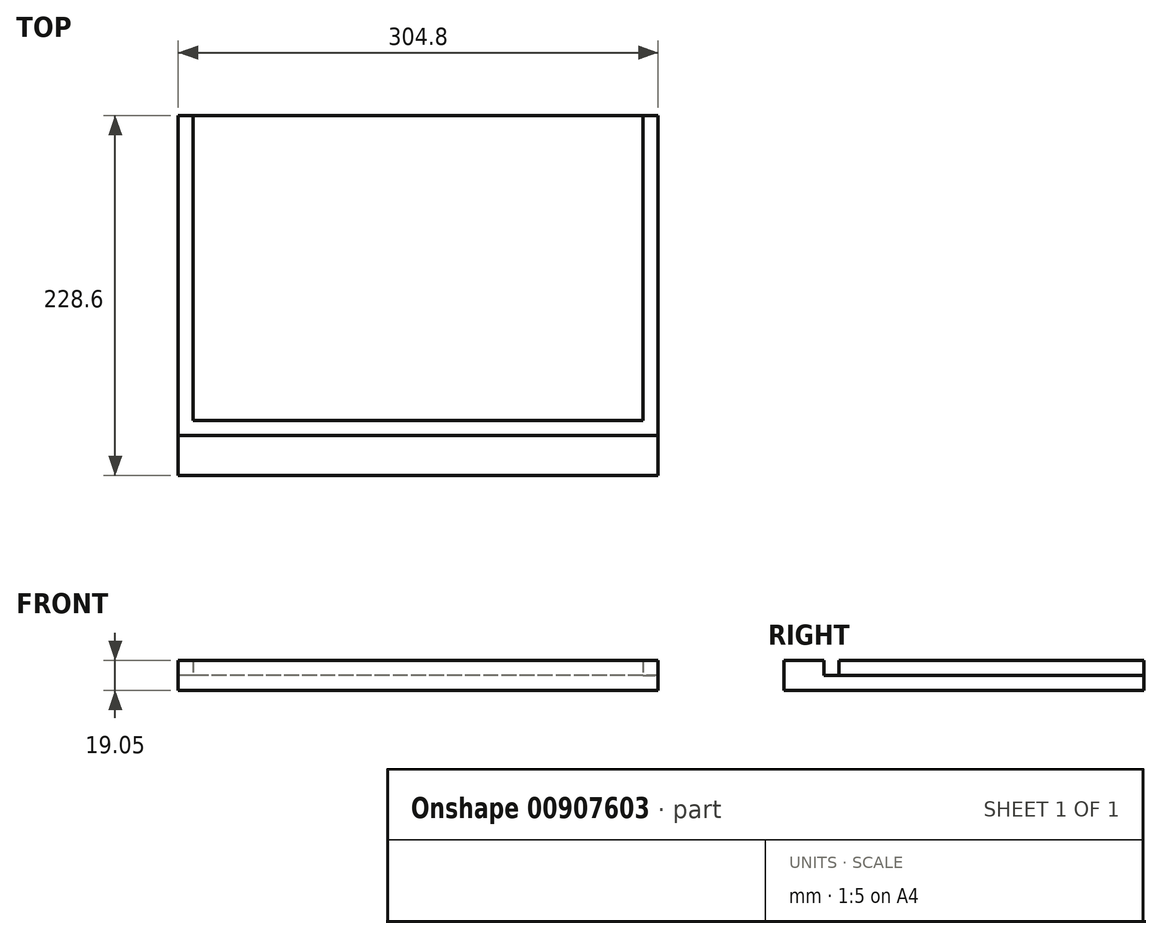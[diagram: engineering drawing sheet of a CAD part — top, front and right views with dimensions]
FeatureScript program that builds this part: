
annotation { "Feature Type Name" : "Feature", "Feature Type Description" : "" }
export const myFeature = defineFeature(function(context is Context, id is Id, definition is map)
    precondition{}
    {
        {
            var Q0;
            Q0=qCreatedBy(makeId("Top.planeOp"),FACE);
            var sketch = newSketch(context, id + "F0", { "sketchPlane" : qUnion([Q0])});
            skLineSegment(sketch, "E0.bottom", {"start": v(152.4, -114.3) * mm, "end": v(-152.4, -114.3) * mm});
            skLineSegment(sketch, "E0.top", {"start": v(152.4, 114.3) * mm, "end": v(-152.4, 114.3) * mm});
            skLineSegment(sketch, "E0.left", {"start": v(152.4, -114.3) * mm, "end": v(152.4, 114.3) * mm});
            skLineSegment(sketch, "E0.right", {"start": v(-152.4, -114.3) * mm, "end": v(-152.4, 114.3) * mm});
            skPoint(sketch, "E0.middle", {"position": v(0, 0) * mm});
            skSolve(sketch);
        }
        {
            var Q0;
            Q0=qSketchRegion(id+"F0",true);
            extrude(context, id + "F1", {"entities" : qUnion([Q0]), "depth" : 19.05 * mm, "offsetDistance" : 25.4 * mm});
        }
        {
            var Q0;
            Q0=makeQuery(id+"F1.opExtrude","CAP_FACE",FACE,{"disambiguationData":[OSD([sQuery(id+"F0.wireOp",EDGE,"E0.bottom"),sQuery(id+"F0.wireOp",EDGE,"E0.top"),sQuery(id+"F0.wireOp",EDGE,"E0.left"),sQuery(id+"F0.wireOp",EDGE,"E0.right")])],"isStart":false});
            var sketch = newSketch(context, id + "F2", { "sketchPlane" : qUnion([Q0])});
            skLineSegment(sketch, "E1", {"start": v(0, -114.3) * mm, "end": v(0, -84.14) * mm});
            skLineSegment(sketch, "E2.bottom", {"start": v(188.14, -79.38) * mm, "end": v(-188.14, -79.38) * mm});
            skLineSegment(sketch, "E2.top", {"start": v(188.14, -88.9) * mm, "end": v(-188.14, -88.9) * mm});
            skLineSegment(sketch, "E2.left", {"start": v(188.14, -79.38) * mm, "end": v(188.14, -88.9) * mm});
            skLineSegment(sketch, "E2.right", {"start": v(-188.14, -79.38) * mm, "end": v(-188.14, -88.9) * mm});
            skPoint(sketch, "E2.middle", {"position": v(0, -84.14) * mm});
            skSolve(sketch);
        }
        {
            var Q0;
            Q0=qSketchRegion(id+"F2",true);
            extrude(context, id + "F3", {"entities" : qUnion([Q0]), "operationType" : NewBodyOperationType.REMOVE, "oppositeDirection" : true, "depth" : 9.52 * mm, "offsetDistance" : 25.4 * mm});
        }
        {
            var Q0;
            Q0=makeQuery(id+"F1.opExtrude","SWEPT_FACE",FACE,{"disambiguationData":[OSD([sQuery(id+"F0.wireOp",EDGE,"E0.right")])]});
            var sketch = newSketch(context, id + "F4", { "sketchPlane" : qUnion([Q0])});
            skLineSegment(sketch, "E3.bottom", {"start": v(79.38, 28.57) * mm, "end": v(-114.3, 28.57) * mm});
            skLineSegment(sketch, "E3.top", {"start": v(79.38, 9.53) * mm, "end": v(-114.3, 9.53) * mm});
            skLineSegment(sketch, "E3.left", {"start": v(79.38, 28.57) * mm, "end": v(79.38, 9.53) * mm});
            skLineSegment(sketch, "E3.right", {"start": v(-114.3, 28.57) * mm, "end": v(-114.3, 9.53) * mm});
            skPoint(sketch, "E3.middle", {"position": v(-17.46, 19.05) * mm});
            skSolve(sketch);
        }
        {
            var Q0;
            Q0=qSketchRegion(id+"F4",true);
            extrude(context, id + "F5", {"entities" : qUnion([Q0]), "operationType" : NewBodyOperationType.REMOVE, "oppositeDirection" : true, "depth" : 9.52 * mm, "offsetDistance" : 25.4 * mm});
        }
        {
            var Q0;
            Q0=makeQuery(id+"F1.opExtrude","SWEPT_FACE",FACE,{"disambiguationData":[OSD([sQuery(id+"F0.wireOp",EDGE,"E0.left")])]});
            var sketch = newSketch(context, id + "F6", { "sketchPlane" : qUnion([Q0])});
            skLineSegment(sketch, "E4.bottom", {"start": v(114.3, 28.57) * mm, "end": v(-79.38, 28.57) * mm});
            skLineSegment(sketch, "E4.top", {"start": v(114.3, 9.53) * mm, "end": v(-79.38, 9.53) * mm});
            skLineSegment(sketch, "E4.left", {"start": v(114.3, 28.57) * mm, "end": v(114.3, 9.53) * mm});
            skLineSegment(sketch, "E4.right", {"start": v(-79.38, 28.57) * mm, "end": v(-79.38, 9.53) * mm});
            skPoint(sketch, "E4.middle", {"position": v(17.46, 19.05) * mm});
            skSolve(sketch);
        }
        {
            var Q0;
            Q0=qSketchRegion(id+"F6",true);
            extrude(context, id + "F7", {"entities" : qUnion([Q0]), "operationType" : NewBodyOperationType.REMOVE, "oppositeDirection" : true, "depth" : 9.52 * mm, "offsetDistance" : 25.4 * mm});
        }
    });
